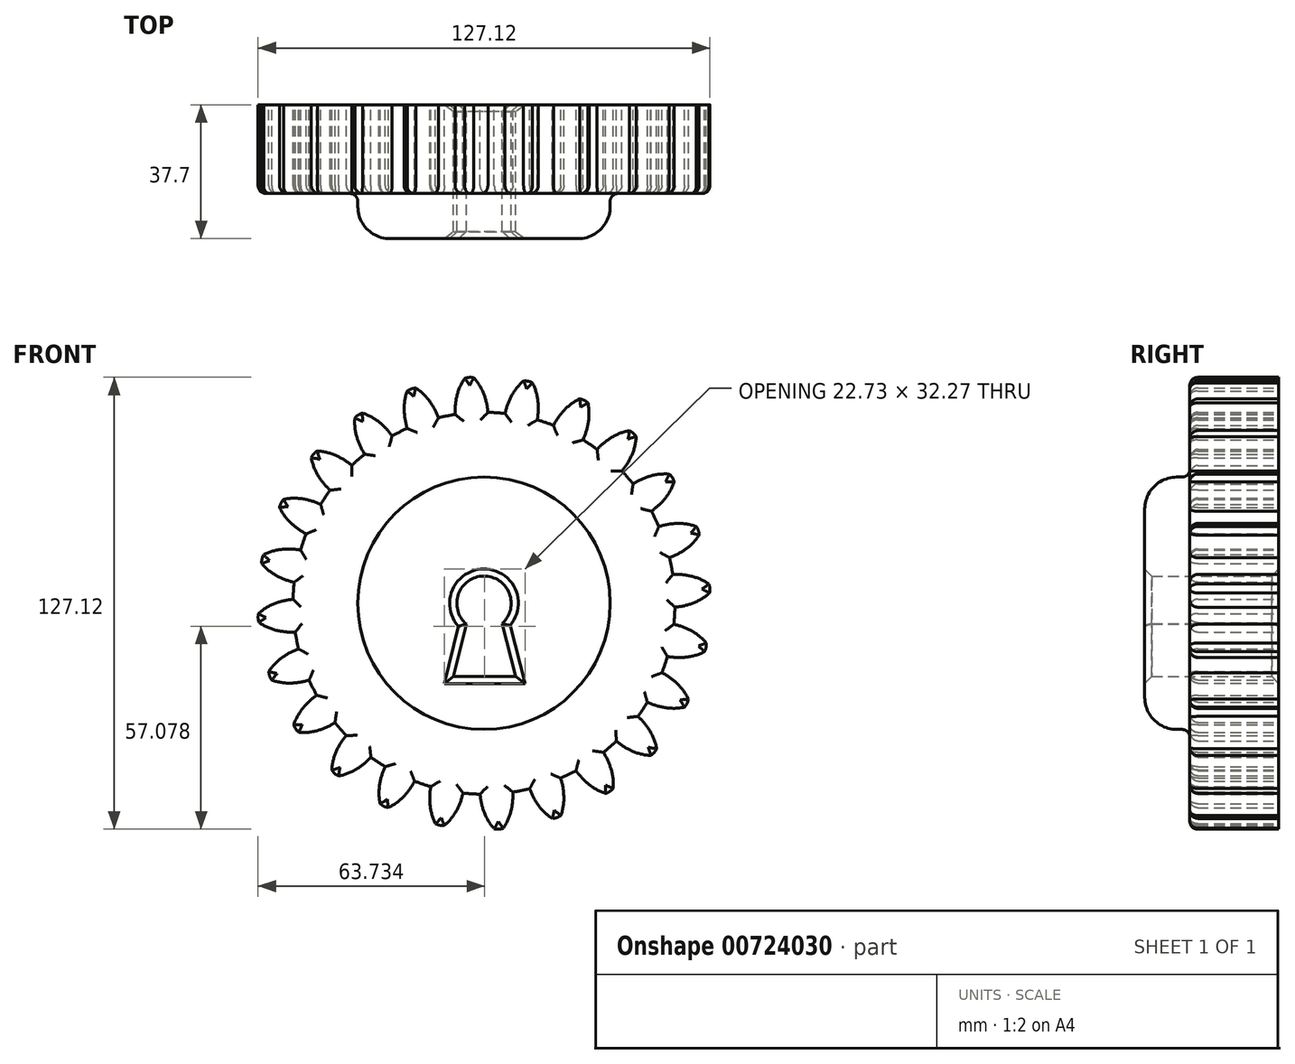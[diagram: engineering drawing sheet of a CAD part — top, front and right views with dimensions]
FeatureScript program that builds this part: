
annotation { "Feature Type Name" : "Feature", "Feature Type Description" : "" }
export const myFeature = defineFeature(function(context is Context, id is Id, definition is map)
    precondition{}
    {
        {
            var Q0;
            Q0=qCreatedBy(makeId("Front.planeOp"),FACE);
            var sketch = newSketch(context, id + "F0", { "sketchPlane" : qUnion([Q0])});
            skCircle(sketch, "E0", {"center": v(0, 0) * mm, "radius": 53.72 * mm});
            skCircle(sketch, "E1", {"center": v(0, 0) * mm, "radius": 58.67 * mm, "construction": true});
            skCircle(sketch, "E2", {"center": v(0, 0) * mm, "radius": 63.5 * mm, "construction": true});
            skLineSegment(sketch, "E3", {"start": v(0, 0) * mm, "end": v(0, 91.84) * mm, "construction": true});
            skLineSegment(sketch, "E4", {"start": v(0, 0) * mm, "end": v(-7.41, 113.09) * mm, "construction": true});
            skLineSegment(sketch, "E5", {"start": v(0, 58.67) * mm, "end": v(-83.5, 56.59) * mm, "construction": true});
            skLineSegment(sketch, "E6", {"start": v(0, 58.67) * mm, "end": v(-75.39, 29.08) * mm, "construction": true});
            skCircle(sketch, "E7", {"center": v(0, 0) * mm, "radius": 54.62 * mm, "construction": true});
            skCircle(sketch, "E8", {"center": v(0, 58.67) * mm, "radius": 16.52 * mm, "construction": true});
            skCircle(sketch, "E9", {"center": v(-15.38, 52.64) * mm, "radius": 16.52 * mm, "construction": true});
            skArc(sketch, "E10", {"start": v(0, 58.67) * mm, "mid": v(-1.21, 61.19) * mm, "end": v(-2.87, 63.43) * mm});
            skArc(sketch, "E11", {"start": v(1.1, 53.7) * mm, "mid": v(0.72, 56.23) * mm, "end": v(0, 58.67) * mm});
            skArc(sketch, "E12.MirrorCS", {"start": v(-8.1, 53.1) * mm, "mid": v(-8.06, 55.65) * mm, "end": v(-7.66, 58.17) * mm});
            skArc(sketch, "E13.MirrorCS", {"start": v(-7.66, 58.17) * mm, "mid": v(-6.78, 60.82) * mm, "end": v(-5.43, 63.27) * mm});
            skArc(sketch, "E14", {"start": v(-2.87, 63.43) * mm, "mid": v(-4.17, 63.55) * mm, "end": v(-5.43, 63.27) * mm});
            skCircle(sketch, "E15", {"center": v(0, 0) * mm, "radius": 35.5 * mm});
            skCircle(sketch, "E16", {"center": v(0, 0) * mm, "radius": 7.65 * mm});
            skLineSegment(sketch, "E17", {"start": v(-4.97, -5.82) * mm, "end": v(-8.64, -20.62) * mm});
            skLineSegment(sketch, "E18", {"start": v(-8.64, -20.62) * mm, "end": v(8.96, -20.62) * mm});
            skLineSegment(sketch, "E19", {"start": v(8.96, -20.62) * mm, "end": v(5.14, -5.67) * mm});
            skSolve(sketch);
        }
        {
            var Q0;
            {var subQ0=sQuery(id+"F0.wireOp",EDGE,"E0");var subQ1=makeQuery(id+"F0.imprint","INTERSECT",VERTEX,{"derivedFrom":[subQ0,sQuery(id+"F0.wireOp",EDGE,"E11")]});Q0=makeQuery(id+"F0.imprint","IMPRINT",FACE,{"disambiguationData":[TD([[makeQuery(id+"F0.imprint","IMPRINT",EDGE,{"disambiguationData":[TD([[subQ1,-1.0]])],"derivedFrom":subQ0}),1.0]])]});}
            var Q1;
            Q1=makeQuery(id+"F0.imprint","IMPRINT",FACE,{"disambiguationData":[TD([[makeQuery(id+"F0.imprint","IMPRINT",EDGE,{"derivedFrom":sQuery(id+"F0.wireOp",EDGE,"E10")}),1.0]])]});
            extrude(context, id + "F1", {"entities" : qUnion([Q0, Q1]), "depth" : 25 * mm, "offsetDistance" : 25 * mm});
        }
        {
            var Q0;
            Q0=makeQuery(id+"F1.opExtrude","SWEPT_BODY",BODY,{"disambiguationData":[OSD([sQuery(id+"F0.wireOp",EDGE,"E0"),sQuery(id+"F0.wireOp",EDGE,"E10"),sQuery(id+"F0.wireOp",EDGE,"E11"),sQuery(id+"F0.wireOp",EDGE,"E12.MirrorCS"),sQuery(id+"F0.wireOp",EDGE,"E13.MirrorCS"),sQuery(id+"F0.wireOp",EDGE,"E14")])]});
            var Q1;
            Q1=makeQuery(id+"F1.opExtrude","SWEPT_FACE",FACE,{"disambiguationData":[OSD([sQuery(id+"F0.wireOp",EDGE,"E0")])]});
            circularPattern(context, id + "F2", {"entities" : qUnion([Q0]), "axis" : qUnion([Q1]), "angle" : 360 * degree, "instanceCount" : 24, "equalSpace" : true});
        }
        {
            var Q0;
            Q0=makeQuery(id+"F0.imprint","IMPRINT",FACE,{"disambiguationData":[TD([[makeQuery(id+"F0.imprint","IMPRINT",EDGE,{"derivedFrom":sQuery(id+"F0.wireOp",EDGE,"E15")}),1.0]])]});
            extrude(context, id + "F3", {"entities" : qUnion([Q0]), "operationType" : NewBodyOperationType.ADD, "depth" : 37.7 * mm, "offsetDistance" : 25 * mm});
        }
        {
            var Q0;
            {var subQ0=makeQuery(id+"F1.opExtrude","CAP_FACE",FACE,{"disambiguationData":[OSD([sQuery(id+"F0.wireOp",EDGE,"E0"),sQuery(id+"F0.wireOp",EDGE,"E10"),sQuery(id+"F0.wireOp",EDGE,"E11"),sQuery(id+"F0.wireOp",EDGE,"E12.MirrorCS"),sQuery(id+"F0.wireOp",EDGE,"E13.MirrorCS"),sQuery(id+"F0.wireOp",EDGE,"E14"),sQuery(id+"F0.wireOp",EDGE,"E15")])],"isStart":false});Q0=makeQuery(id+"F3.boolean.opBoolean","MERGE",FACE,{"derivedFrom":[subQ0,makeQuery(id+"F2.opPattern","COPY",FACE,{"derivedFrom":subQ0,"instanceName":"1"}),makeQuery(id+"F2.opPattern","COPY",FACE,{"derivedFrom":subQ0,"instanceName":"2"}),makeQuery(id+"F2.opPattern","COPY",FACE,{"derivedFrom":subQ0,"instanceName":"3"}),makeQuery(id+"F2.opPattern","COPY",FACE,{"derivedFrom":subQ0,"instanceName":"4"}),makeQuery(id+"F2.opPattern","COPY",FACE,{"derivedFrom":subQ0,"instanceName":"5"}),makeQuery(id+"F2.opPattern","COPY",FACE,{"derivedFrom":subQ0,"instanceName":"6"}),makeQuery(id+"F2.opPattern","COPY",FACE,{"derivedFrom":subQ0,"instanceName":"7"}),makeQuery(id+"F2.opPattern","COPY",FACE,{"derivedFrom":subQ0,"instanceName":"8"}),makeQuery(id+"F2.opPattern","COPY",FACE,{"derivedFrom":subQ0,"instanceName":"9"}),makeQuery(id+"F2.opPattern","COPY",FACE,{"derivedFrom":subQ0,"instanceName":"10"}),makeQuery(id+"F2.opPattern","COPY",FACE,{"derivedFrom":subQ0,"instanceName":"11"}),makeQuery(id+"F2.opPattern","COPY",FACE,{"derivedFrom":subQ0,"instanceName":"12"}),makeQuery(id+"F2.opPattern","COPY",FACE,{"derivedFrom":subQ0,"instanceName":"13"}),makeQuery(id+"F2.opPattern","COPY",FACE,{"derivedFrom":subQ0,"instanceName":"14"}),makeQuery(id+"F2.opPattern","COPY",FACE,{"derivedFrom":subQ0,"instanceName":"15"}),makeQuery(id+"F2.opPattern","COPY",FACE,{"derivedFrom":subQ0,"instanceName":"16"}),makeQuery(id+"F2.opPattern","COPY",FACE,{"derivedFrom":subQ0,"instanceName":"17"}),makeQuery(id+"F2.opPattern","COPY",FACE,{"derivedFrom":subQ0,"instanceName":"18"}),makeQuery(id+"F2.opPattern","COPY",FACE,{"derivedFrom":subQ0,"instanceName":"19"}),makeQuery(id+"F2.opPattern","COPY",FACE,{"derivedFrom":subQ0,"instanceName":"20"}),makeQuery(id+"F2.opPattern","COPY",FACE,{"derivedFrom":subQ0,"instanceName":"21"}),makeQuery(id+"F2.opPattern","COPY",FACE,{"derivedFrom":subQ0,"instanceName":"22"}),makeQuery(id+"F2.opPattern","COPY",FACE,{"derivedFrom":subQ0,"instanceName":"23"})]});}
            fillet(context, id + "F4", {"entities" : qUnion([Q0]), "radius" : 2.2 * mm, "tangentPropagation" : true, "allowEdgeOverflow" : false});
        }
        {
            var Q0;
            Q0=makeQuery(id+"F3.opExtrude","CAP_EDGE",EDGE,{"disambiguationData":[OSD([sQuery(id+"F0.wireOp",EDGE,"E15")])],"isStart":false});
            fillet(context, id + "F5", {"entities" : qUnion([Q0]), "radius" : 9 * mm, "tangentPropagation" : true, "allowEdgeOverflow" : false});
        }
        {
            var Q0;
            Q0=makeQuery(id+"F3.opExtrude","CAP_EDGE",EDGE,{"disambiguationData":[OSD([sQuery(id+"F0.wireOp",EDGE,"E16")])],"isStart":false});
            var Q1;
            Q1=makeQuery(id+"F3.opExtrude","CAP_EDGE",EDGE,{"disambiguationData":[OSD([sQuery(id+"F0.wireOp",EDGE,"E17")])],"isStart":false});
            var Q2;
            Q2=makeQuery(id+"F3.opExtrude","CAP_EDGE",EDGE,{"disambiguationData":[OSD([sQuery(id+"F0.wireOp",EDGE,"E19")])],"isStart":false});
            var Q3;
            Q3=makeQuery(id+"F3.opExtrude","CAP_EDGE",EDGE,{"disambiguationData":[OSD([sQuery(id+"F0.wireOp",EDGE,"E18")])],"isStart":false});
            var Q4;
            Q4=makeQuery(id+"F3.opExtrude","CAP_EDGE",EDGE,{"disambiguationData":[OSD([sQuery(id+"F0.wireOp",EDGE,"E16")])],"isStart":true});
            var Q5;
            Q5=makeQuery(id+"F3.opExtrude","CAP_EDGE",EDGE,{"disambiguationData":[OSD([sQuery(id+"F0.wireOp",EDGE,"E17")])],"isStart":true});
            var Q6;
            Q6=makeQuery(id+"F3.opExtrude","CAP_EDGE",EDGE,{"disambiguationData":[OSD([sQuery(id+"F0.wireOp",EDGE,"E18")])],"isStart":true});
            var Q7;
            Q7=makeQuery(id+"F3.opExtrude","CAP_EDGE",EDGE,{"disambiguationData":[OSD([sQuery(id+"F0.wireOp",EDGE,"E19")])],"isStart":true});
            chamfer(context, id + "F6", {"entities" : qUnion([Q0, Q1, Q2, Q3, Q4, Q5, Q6, Q7]), "width" : 2 * mm, "tangentPropagation" : true});
        }
    });
